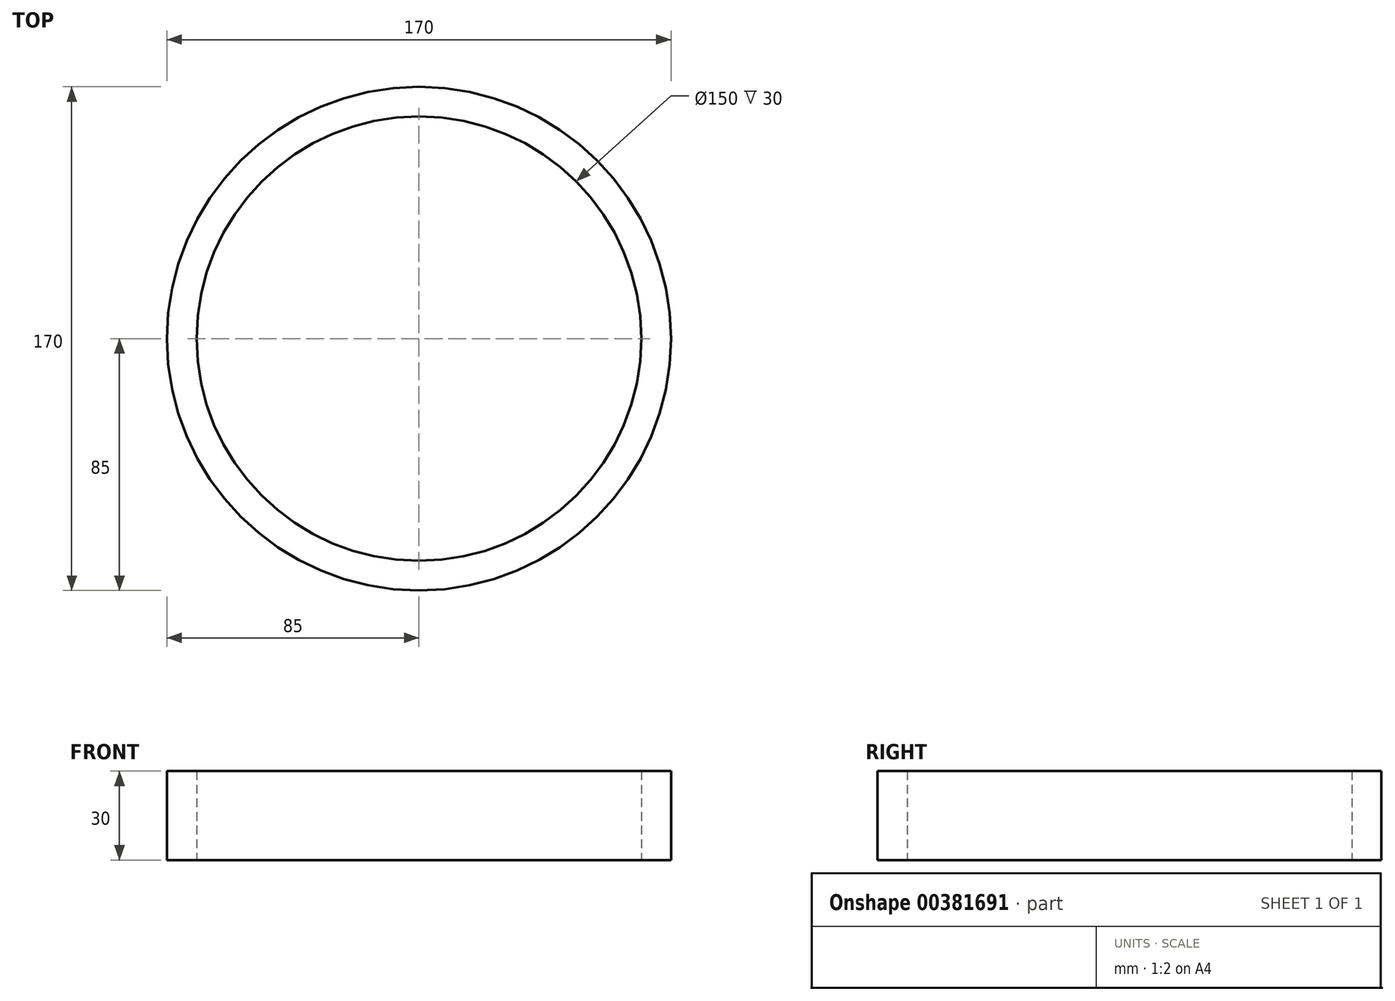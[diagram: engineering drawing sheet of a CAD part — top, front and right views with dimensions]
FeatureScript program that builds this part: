
annotation { "Feature Type Name" : "Feature", "Feature Type Description" : "" }
export const myFeature = defineFeature(function(context is Context, id is Id, definition is map)
    precondition{}
    {
        {
            var Q0;
            Q0=qCreatedBy(makeId("Top.planeOp"),FACE);
            var sketch = newSketch(context, id + "F0", { "sketchPlane" : qUnion([Q0])});
            skCircle(sketch, "E0", {"center": v(0, 0) * mm, "radius": 75 * mm});
            skCircle(sketch, "E1", {"center": v(0, 0) * mm, "radius": 85 * mm});
            skSolve(sketch);
        }
        {
            var Q0;
            Q0 = qSketchRegion(id + "F0", true);
            extrude(context, id + "F1", {"entities" : qUnion([Q0]), "depth" : 30 * mm});
        }
    });
